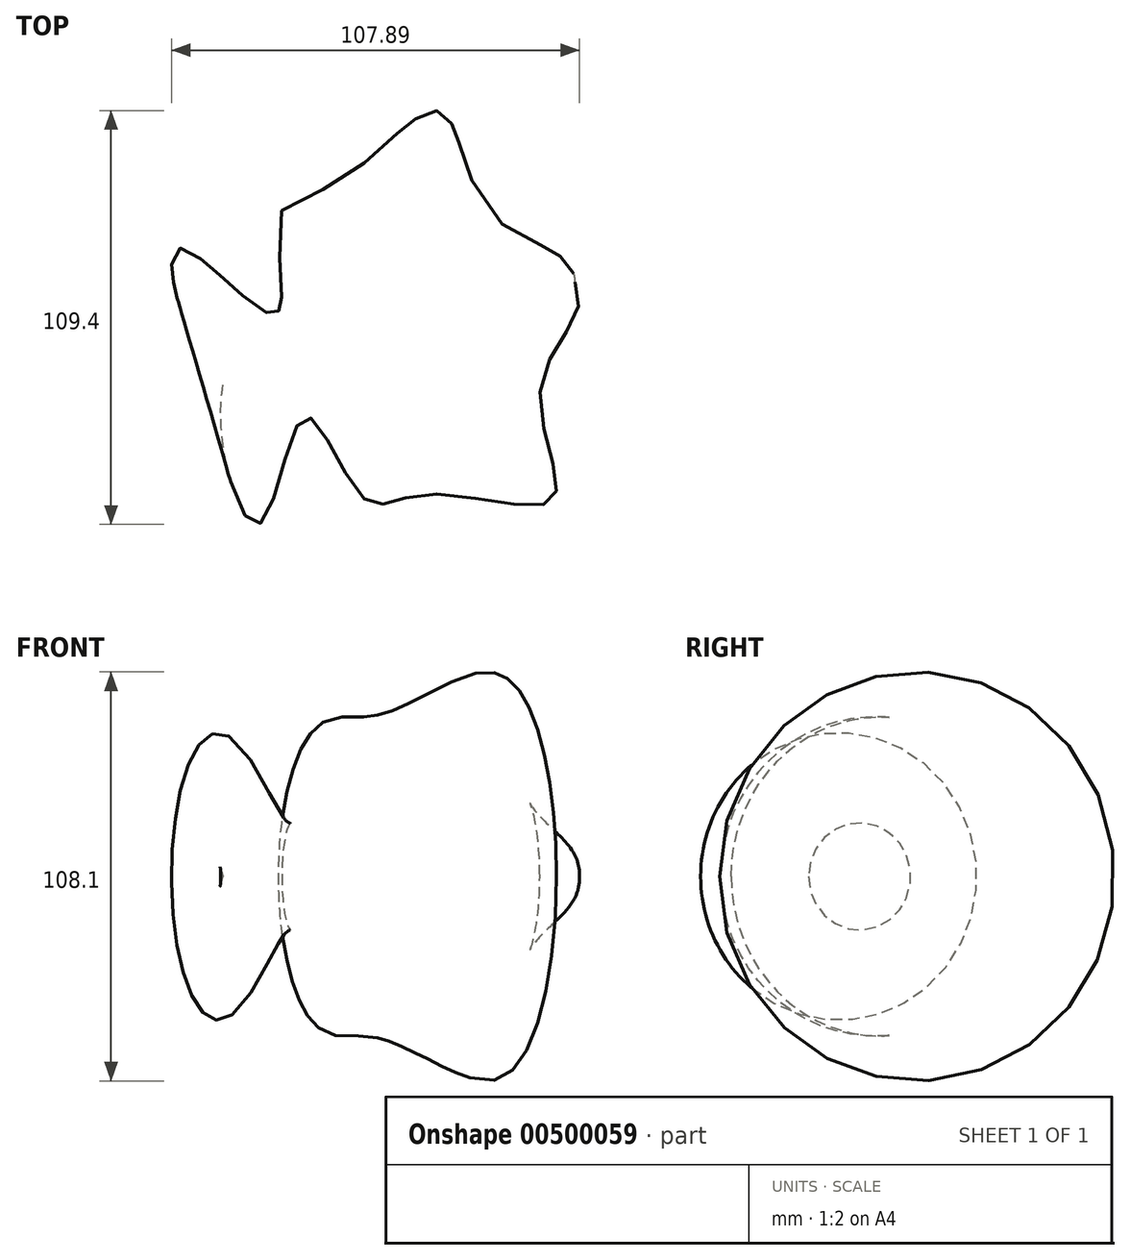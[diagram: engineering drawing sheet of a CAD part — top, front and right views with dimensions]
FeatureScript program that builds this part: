
annotation { "Feature Type Name" : "Feature", "Feature Type Description" : "" }
export const myFeature = defineFeature(function(context is Context, id is Id, definition is map)
    precondition{}
    {
        {
            var Q0;
            Q0=qCreatedBy(makeId("Top.planeOp"),FACE);
            var sketch = newSketch(context, id + "F0", { "sketchPlane" : qUnion([Q0])});
            skFitSpline(sketch, "E0", {"points": [v(-56.84, 9.47) * mm, v(-43.14, 50.86) * mm, v(-42.85, 49.11) * mm, v(-35.56, 15.3) * mm, v(-35.27, 15.01) * mm, v(10.5, 29) * mm, v(11.37, 24.34) * mm, v(25.94, 5.98) * mm, v(15.74, -19.38) * mm, v(18.95, -48.82) * mm, v(-14.87, -47.36) * mm, v(-30.9, -48.53) * mm, v(-46.64, -26.96) * mm, v(-58.59, -55.23) * mm, v(-67.04, -14.43) * mm, v(-51.6, 2.48) * mm, v(-56.84, 9.47) * mm]});
            skLineSegment(sketch, "E1", {"start": v(-128.9, -36.23) * mm, "end": v(102.5, 31.32) * mm});
            skSolve(sketch);
        }
        {
            var Q0;
            {var subQ0=sQuery(id+"F0.wireOp",EDGE,"E1");var subQ1=sQuery(id+"F0.wireOp",EDGE,"E0");var subQ2=makeQuery(id+"F0.imprint","INTERSECT",VERTEX,{"disambiguationData":[OD(0.0)],"derivedFrom":[subQ1,subQ0]});Q0=makeQuery(id+"F0.imprint","IMPRINT",FACE,{"disambiguationData":[TD([[makeQuery(id+"F0.imprint","IMPRINT",EDGE,{"disambiguationData":[TD([[subQ2,-1.0]])],"derivedFrom":subQ1}),-1.0]])]});}
            var Q1;
            Q1=sQuery(id+"F0.wireOp",EDGE,"E1");
            revolve(context, id + "F1", {"entities" : qUnion([Q0]), "axis" : qUnion([Q1]), "revolveType" : RevolveType.FULL});
        }
    });
